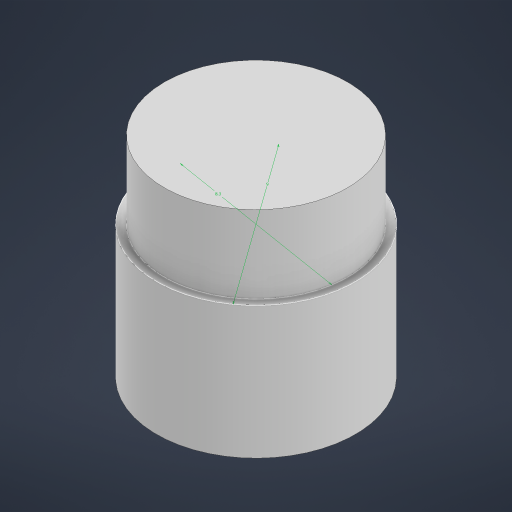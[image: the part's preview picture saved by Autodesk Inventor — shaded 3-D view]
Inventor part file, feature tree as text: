
AUTODESK INVENTOR PART (.ipt)
format: ipt  version: 2023 (Build 270158000, 158)  size: 171,008 bytes
history: native  units: mm
features: extrude x2, sketch x1
ambient origin geometry x8: Origin, YZ Plane, XZ Plane, XY Plane, X Axis, Y Axis, Z Axis, Center Point
bodies: Solid1 (feature_tree)
feature tree (3):
  sketch  "Sketch1"  dims[d0=9.0mm d1=8.3mm d2=3.5mm d3=0.0mm d4=6.0mm d5=0.0mm]
  extrude  "Extrusion1"  Depth=6.0mm
  extrude  "Extrusion2"  Depth=3.5mm TaperAngle=0.0deg
